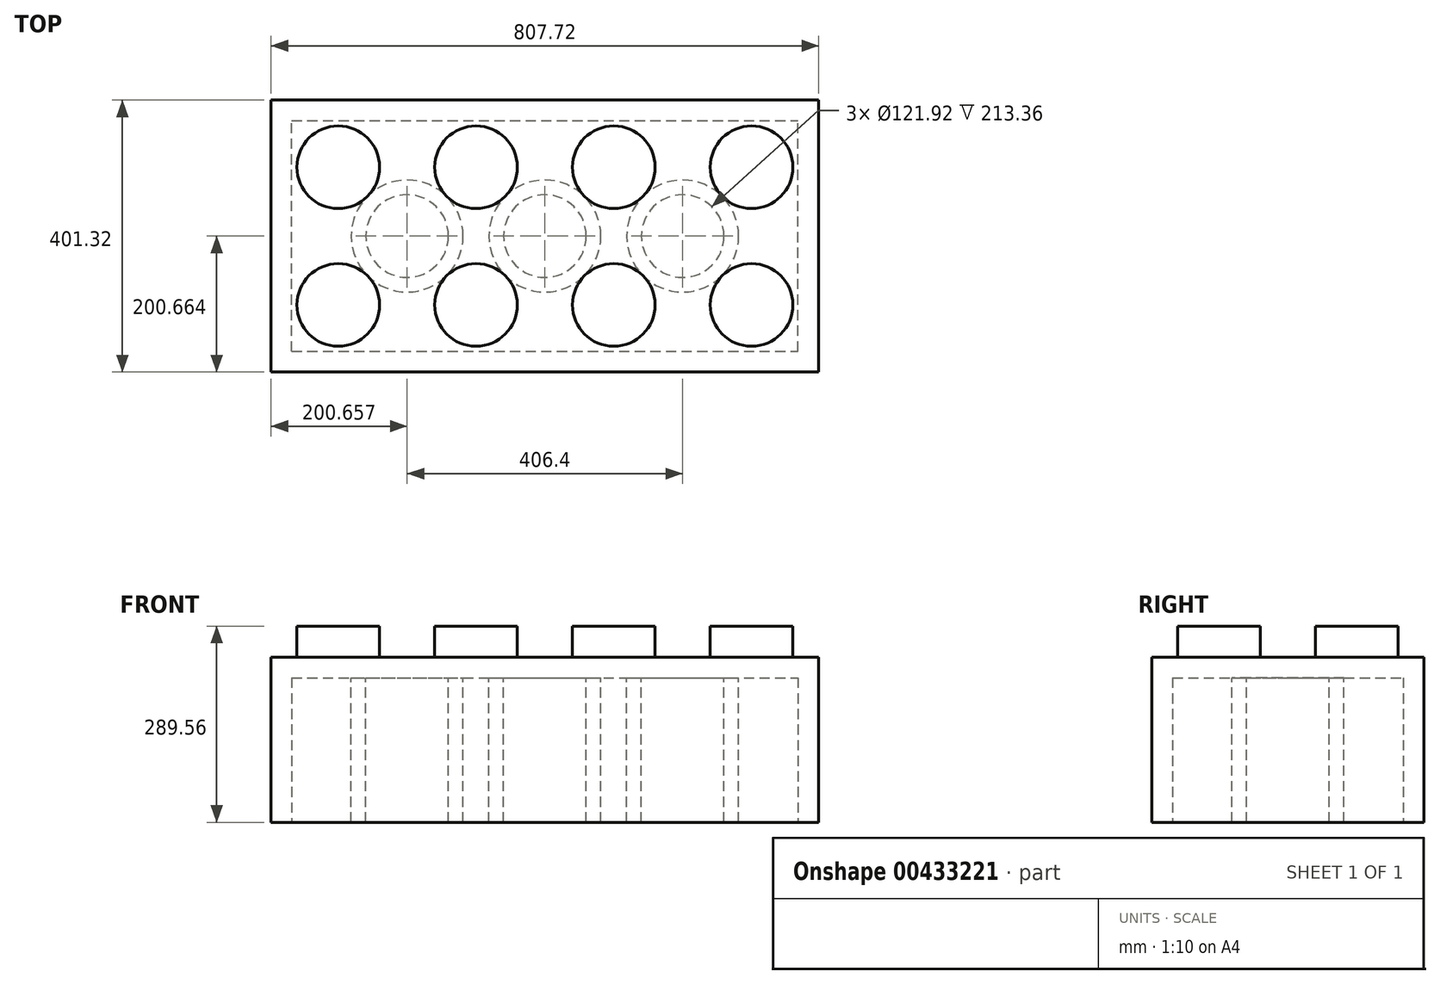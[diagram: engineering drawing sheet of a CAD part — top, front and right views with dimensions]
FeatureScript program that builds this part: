
annotation { "Feature Type Name" : "Feature", "Feature Type Description" : "" }
export const myFeature = defineFeature(function(context is Context, id is Id, definition is map)
    precondition{}
    {
        {
            var Q0;
            Q0=qCreatedBy(makeId("Top.planeOp"),FACE);
            var sketch = newSketch(context, id + "F0", { "sketchPlane" : qUnion([Q0])});
            skLineSegment(sketch, "E0.bottom", {"start": v(-380.42, 188.02) * mm, "end": v(427.3, 188.02) * mm});
            skLineSegment(sketch, "E0.top", {"start": v(-380.42, -213.3) * mm, "end": v(427.3, -213.3) * mm});
            skLineSegment(sketch, "E0.left", {"start": v(-380.42, 188.02) * mm, "end": v(-380.42, -213.3) * mm});
            skLineSegment(sketch, "E0.right", {"start": v(427.3, 188.02) * mm, "end": v(427.3, -213.3) * mm});
            skSolve(sketch);
        }
        {
            var Q0;
            Q0=makeQuery(id+"F0.imprint","IMPRINT",FACE,{"disambiguationData":[TD([[makeQuery(id+"F0.imprint","IMPRINT",EDGE,{"derivedFrom":sQuery(id+"F0.wireOp",EDGE,"E0.bottom")}),-1.0]])]});
            extrude(context, id + "F1", {"entities" : qUnion([Q0]), "depth" : 243.84 * mm});
        }
        {
            var Q0;
            Q0=makeQuery(id+"F1.opExtrude","CAP_FACE",FACE,{"disambiguationData":[OSD([sQuery(id+"F0.wireOp",EDGE,"E0.bottom"),sQuery(id+"F0.wireOp",EDGE,"E0.top"),sQuery(id+"F0.wireOp",EDGE,"E0.left"),sQuery(id+"F0.wireOp",EDGE,"E0.right")])],"isStart":true});
            var sketch = newSketch(context, id + "F2", { "sketchPlane" : qUnion([Q0])});
            skLineSegment(sketch, "E1.bottom", {"start": v(-349.94, 182.82) * mm, "end": v(396.82, 182.82) * mm});
            skLineSegment(sketch, "E1.top", {"start": v(-349.94, -157.54) * mm, "end": v(396.82, -157.54) * mm});
            skLineSegment(sketch, "E1.left", {"start": v(-349.94, 182.82) * mm, "end": v(-349.94, -157.54) * mm});
            skLineSegment(sketch, "E2", {"start": v(396.82, 182.82) * mm, "end": v(396.82, -157.54) * mm});
            skSolve(sketch);
        }
        {
            var Q0;
            Q0=makeQuery(id+"F1.opExtrude","CAP_FACE",FACE,{"disambiguationData":[OSD([sQuery(id+"F0.wireOp",EDGE,"E0.bottom"),sQuery(id+"F0.wireOp",EDGE,"E0.top"),sQuery(id+"F0.wireOp",EDGE,"E0.left"),sQuery(id+"F0.wireOp",EDGE,"E0.right")])],"isStart":false});
            var sketch = newSketch(context, id + "F3", { "sketchPlane" : qUnion([Q0])});
            skCircle(sketch, "E3", {"center": v(-281.36, 88.96) * mm, "radius": 60.96 * mm});
            skCircle(sketch, "E4.1.0.0", {"center": v(-78.16, 88.96) * mm, "radius": 60.96 * mm});
            skCircle(sketch, "E4.2.0.0", {"center": v(125.04, 88.96) * mm, "radius": 60.96 * mm});
            skCircle(sketch, "E4.3.0.0", {"center": v(328.24, 88.96) * mm, "radius": 60.96 * mm});
            skLineSegment(sketch, "E4.direction1", {"start": v(-281.36, 88.96) * mm, "end": v(-78.16, 88.96) * mm, "construction": true});
            skCircle(sketch, "E5.0.1.0", {"center": v(-281.36, -114.24) * mm, "radius": 60.96 * mm});
            skCircle(sketch, "E5.1.1.0", {"center": v(-78.16, -114.24) * mm, "radius": 60.96 * mm});
            skCircle(sketch, "E5.2.1.0", {"center": v(125.04, -114.24) * mm, "radius": 60.96 * mm});
            skCircle(sketch, "E5.3.1.0", {"center": v(328.24, -114.24) * mm, "radius": 60.96 * mm});
            skLineSegment(sketch, "E5.direction2", {"start": v(-281.36, 88.96) * mm, "end": v(-281.36, -114.24) * mm, "construction": true});
            skSolve(sketch);
        }
        {
            var Q0;
            Q0=makeQuery(id+"F3.imprint","IMPRINT",FACE,{"disambiguationData":[TD([[makeQuery(id+"F3.imprint","IMPRINT",EDGE,{"derivedFrom":sQuery(id+"F3.wireOp",EDGE,"E3")}),1.0]])]});
            var Q1;
            Q1=makeQuery(id+"F3.imprint","IMPRINT",FACE,{"disambiguationData":[TD([[makeQuery(id+"F3.imprint","IMPRINT",EDGE,{"derivedFrom":sQuery(id+"F3.wireOp",EDGE,"E4.1.0.0")}),1.0]])]});
            var Q2;
            Q2=makeQuery(id+"F3.imprint","IMPRINT",FACE,{"disambiguationData":[TD([[makeQuery(id+"F3.imprint","IMPRINT",EDGE,{"derivedFrom":sQuery(id+"F3.wireOp",EDGE,"E4.2.0.0")}),1.0]])]});
            var Q3;
            Q3=makeQuery(id+"F3.imprint","IMPRINT",FACE,{"disambiguationData":[TD([[makeQuery(id+"F3.imprint","IMPRINT",EDGE,{"derivedFrom":sQuery(id+"F3.wireOp",EDGE,"E4.3.0.0")}),1.0]])]});
            var Q4;
            Q4=makeQuery(id+"F3.imprint","IMPRINT",FACE,{"disambiguationData":[TD([[makeQuery(id+"F3.imprint","IMPRINT",EDGE,{"derivedFrom":sQuery(id+"F3.wireOp",EDGE,"E5.0.1.0")}),1.0]])]});
            var Q5;
            Q5=makeQuery(id+"F3.imprint","IMPRINT",FACE,{"disambiguationData":[TD([[makeQuery(id+"F3.imprint","IMPRINT",EDGE,{"derivedFrom":sQuery(id+"F3.wireOp",EDGE,"E5.1.1.0")}),1.0]])]});
            var Q6;
            Q6=makeQuery(id+"F3.imprint","IMPRINT",FACE,{"disambiguationData":[TD([[makeQuery(id+"F3.imprint","IMPRINT",EDGE,{"derivedFrom":sQuery(id+"F3.wireOp",EDGE,"E5.2.1.0")}),1.0]])]});
            var Q7;
            Q7=makeQuery(id+"F3.imprint","IMPRINT",FACE,{"disambiguationData":[TD([[makeQuery(id+"F3.imprint","IMPRINT",EDGE,{"derivedFrom":sQuery(id+"F3.wireOp",EDGE,"E5.3.1.0")}),1.0]])]});
            extrude(context, id + "F4", {"entities" : qUnion([Q0, Q1, Q2, Q3, Q4, Q5, Q6, Q7]), "operationType" : NewBodyOperationType.ADD, "depth" : 45.72 * mm});
        }
        {
            var Q0;
            Q0=makeQuery(id+"F2.imprint","IMPRINT",FACE,{"disambiguationData":[TD([[makeQuery(id+"F2.imprint","IMPRINT",EDGE,{"derivedFrom":sQuery(id+"F2.wireOp",EDGE,"E1.bottom")}),-1.0]])]});
            extrude(context, id + "F5", {"entities" : qUnion([Q0]), "operationType" : NewBodyOperationType.REMOVE, "oppositeDirection" : true, "depth" : 213.36 * mm});
        }
        {
            var Q0;
            Q0=makeQuery(id+"F5.boolean.opBoolean","COPY",FACE,{"derivedFrom":makeQuery(id+"F5.opExtrude","CAP_FACE",FACE,{"disambiguationData":[OSD([sQuery(id+"F2.wireOp",EDGE,"E1.bottom"),sQuery(id+"F2.wireOp",EDGE,"E1.top"),sQuery(id+"F2.wireOp",EDGE,"E1.left"),sQuery(id+"F2.wireOp",EDGE,"E2")])],"isStart":false})});
            var sketch = newSketch(context, id + "F6", { "sketchPlane" : qUnion([Q0])});
            skCircle(sketch, "E6", {"center": v(23.44, 12.64) * mm, "radius": 82.55 * mm});
            skCircle(sketch, "E7", {"center": v(23.44, 12.64) * mm, "radius": 60.96 * mm});
            skCircle(sketch, "E8.1.0.0", {"center": v(226.64, 12.64) * mm, "radius": 60.96 * mm});
            skCircle(sketch, "E8.1.0.1", {"center": v(226.64, 12.64) * mm, "radius": 82.55 * mm});
            skLineSegment(sketch, "E8.direction1", {"start": v(23.44, 12.64) * mm, "end": v(226.64, 12.64) * mm, "construction": true});
            skCircle(sketch, "E9.1.0.0", {"center": v(-179.76, 12.64) * mm, "radius": 60.96 * mm});
            skCircle(sketch, "E9.1.0.1", {"center": v(-179.76, 12.64) * mm, "radius": 82.55 * mm});
            skLineSegment(sketch, "E9.direction1", {"start": v(23.44, 12.64) * mm, "end": v(-179.76, 12.64) * mm, "construction": true});
            skSolve(sketch);
        }
        {
            var Q0;
            Q0 = qSketchRegion(id + "F6", true);
            extrude(context, id + "F7", {"entities" : qUnion([Q0]), "operationType" : NewBodyOperationType.ADD, "depth" : 213.36 * mm});
        }
    });
